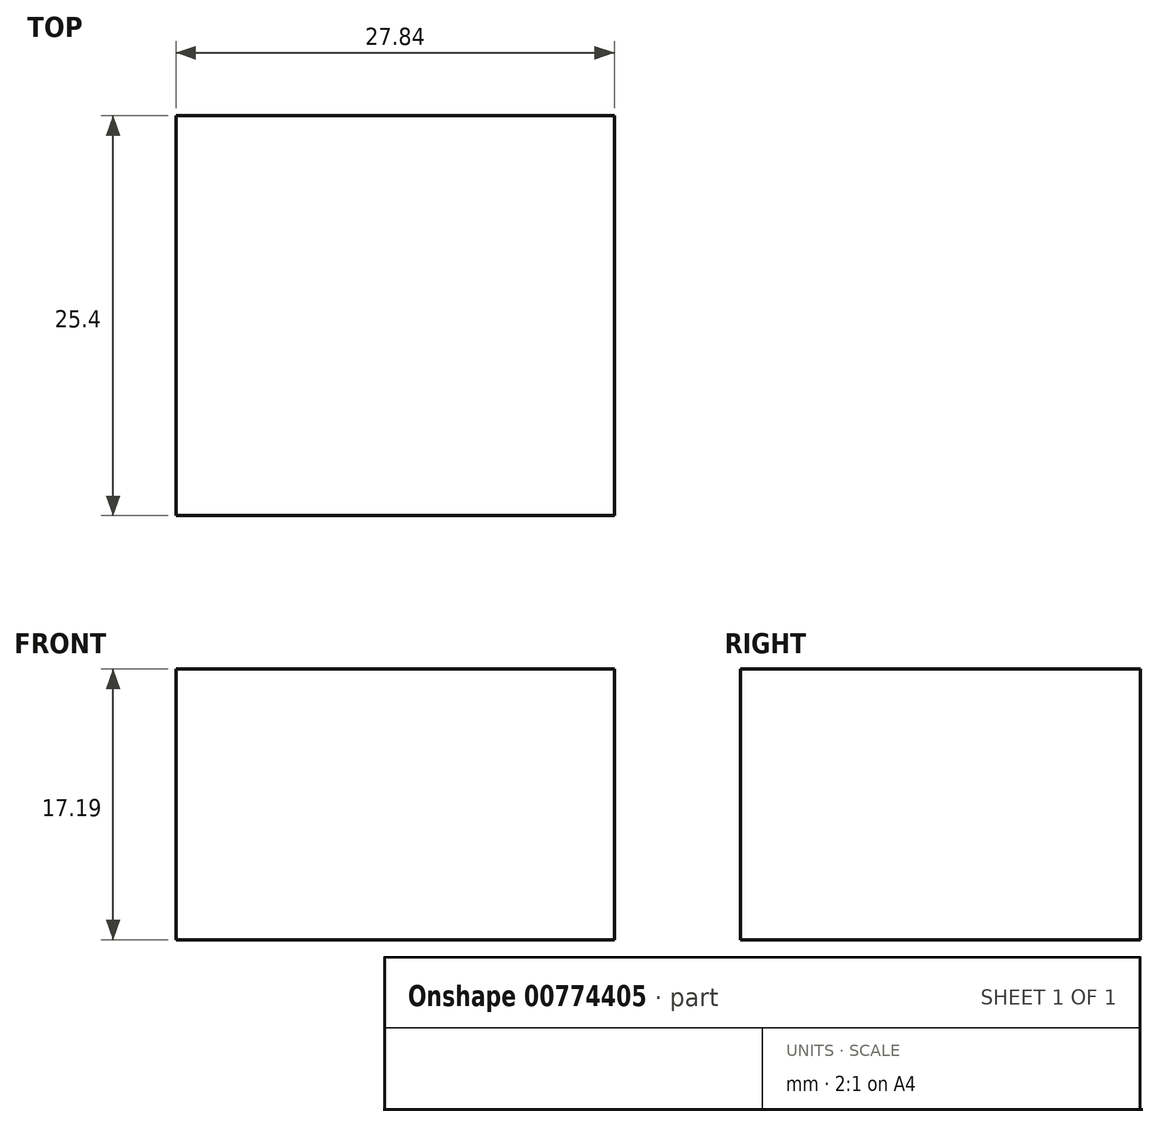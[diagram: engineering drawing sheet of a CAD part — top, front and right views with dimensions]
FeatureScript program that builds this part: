
annotation { "Feature Type Name" : "Feature", "Feature Type Description" : "" }
export const myFeature = defineFeature(function(context is Context, id is Id, definition is map)
    precondition{}
    {
        {
            var Q0;
            Q0=qCreatedBy(makeId("Front.planeOp"),FACE);
            var sketch = newSketch(context, id + "F0", { "sketchPlane" : qUnion([Q0])});
            skLineSegment(sketch, "E0.bottom", {"start": v(0, 0) * mm, "end": v(27.84, 0) * mm});
            skLineSegment(sketch, "E0.top", {"start": v(0, 17.2) * mm, "end": v(27.84, 17.2) * mm});
            skLineSegment(sketch, "E0.left", {"start": v(0, 0) * mm, "end": v(0, 17.2) * mm});
            skLineSegment(sketch, "E0.right", {"start": v(27.84, 0) * mm, "end": v(27.84, 17.2) * mm});
            skSolve(sketch);
        }
        {
            var Q0;
            Q0=makeQuery(id+"F0.imprint","IMPRINT",FACE,{"disambiguationData":[TD([[makeQuery(id+"F0.imprint","IMPRINT",EDGE,{"derivedFrom":sQuery(id+"F0.wireOp",EDGE,"E0.bottom")}),1.0]])]});
            extrude(context, id + "F1", {"entities" : qUnion([Q0]), "depth" : 25.4 * mm, "offsetDistance" : 25.4 * mm});
        }
    });
